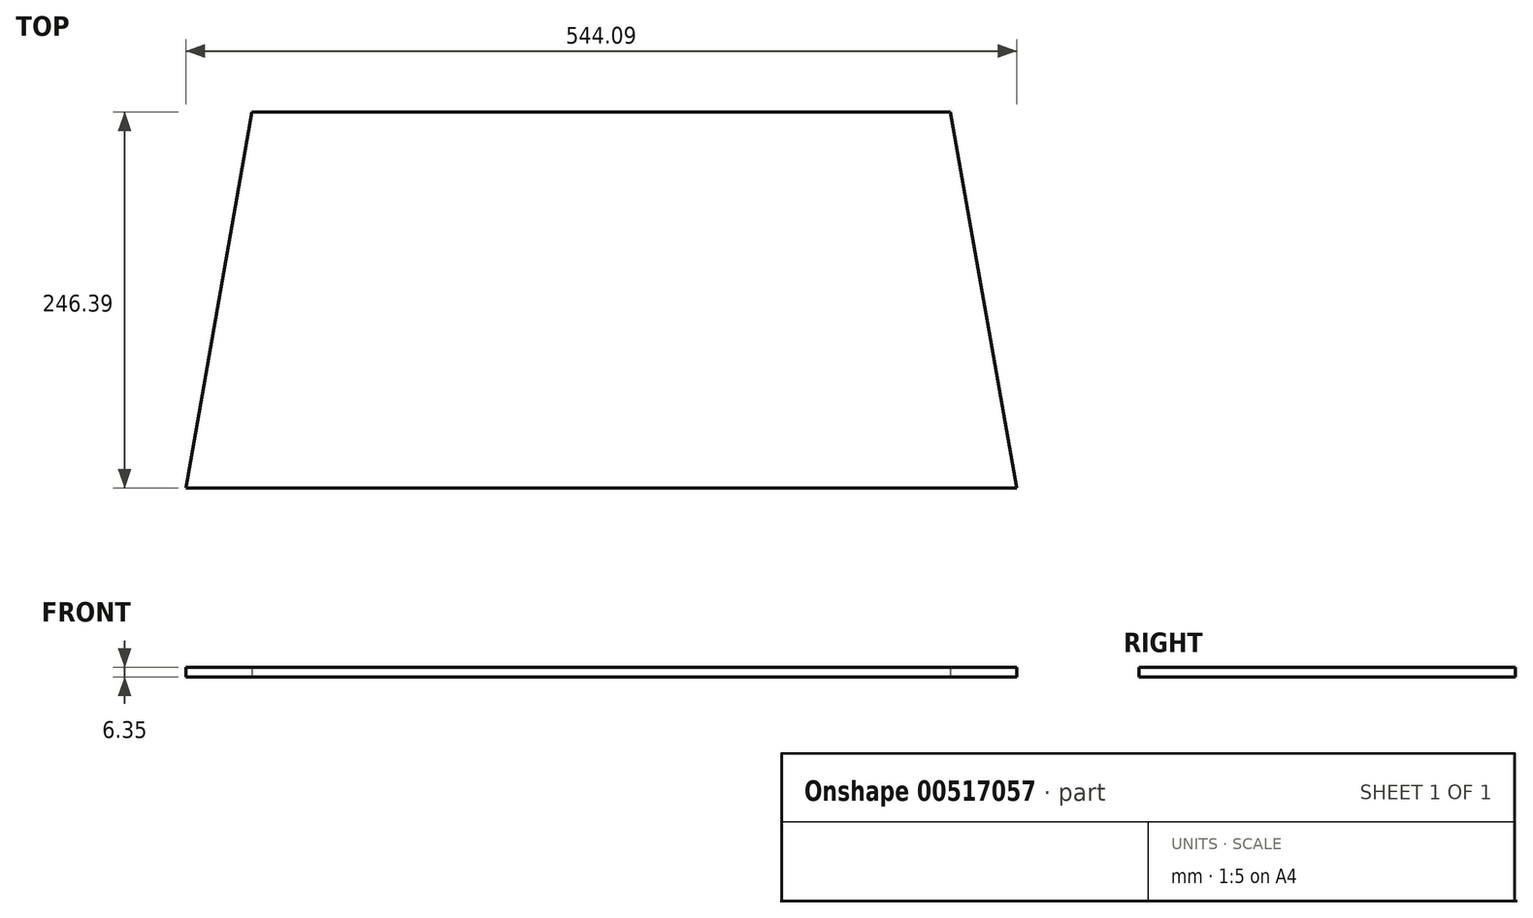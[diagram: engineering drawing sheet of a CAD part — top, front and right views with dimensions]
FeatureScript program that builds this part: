
annotation { "Feature Type Name" : "Feature", "Feature Type Description" : "" }
export const myFeature = defineFeature(function(context is Context, id is Id, definition is map)
    precondition{}
    {
        {
            var Q0;
            Q0=qCreatedBy(makeId("Top.planeOp"),FACE);
            var sketch = newSketch(context, id + "F0", { "sketchPlane" : qUnion([Q0])});
            skLineSegment(sketch, "E0.bottom", {"start": v(-256.12, 169.6) * mm, "end": v(201.08, 169.6) * mm});
            skLineSegment(sketch, "E0.right", {"start": v(201.08, 169.6) * mm, "end": v(244.53, -76.8) * mm});
            skLineSegment(sketch, "E1", {"start": v(-256.12, 169.6) * mm, "end": v(-299.56, -76.8) * mm});
            skLineSegment(sketch, "E2", {"start": v(-299.56, -76.8) * mm, "end": v(244.53, -76.8) * mm});
            skSolve(sketch);
        }
        {
            var Q0;
            Q0=makeQuery(id+"F0.imprint","IMPRINT",FACE,{"disambiguationData":[TD([[makeQuery(id+"F0.imprint","IMPRINT",EDGE,{"derivedFrom":sQuery(id+"F0.wireOp",EDGE,"E0.bottom")}),-1.0]])]});
            extrude(context, id + "F1", {"entities" : qUnion([Q0]), "depth" : 12.7 * mm, "offsetDistance" : 25.4 * mm});
        }
        {
            var Q0;
            Q0=makeQuery(id+"F1.opExtrude","CAP_FACE",FACE,{"disambiguationData":[OSD([sQuery(id+"F0.wireOp",EDGE,"E0.bottom"),sQuery(id+"F0.wireOp",EDGE,"E0.right"),sQuery(id+"F0.wireOp",EDGE,"E1"),sQuery(id+"F0.wireOp",EDGE,"E2")])],"isStart":false});
            extrude(context, id + "F2", {"entities" : qUnion([Q0]), "operationType" : NewBodyOperationType.ADD, "depth" : -6.35 * mm, "offsetDistance" : 25.4 * mm});
        }
        {
            var Q0;
            Q0=makeQuery(id+"F1.opExtrude","CAP_FACE",FACE,{"disambiguationData":[OSD([sQuery(id+"F0.wireOp",EDGE,"E0.bottom"),sQuery(id+"F0.wireOp",EDGE,"E0.right"),sQuery(id+"F0.wireOp",EDGE,"E1"),sQuery(id+"F0.wireOp",EDGE,"E2")])],"isStart":false});
            extrude(context, id + "F3", {"entities" : qUnion([Q0]), "operationType" : NewBodyOperationType.ADD, "depth" : -6.35 * mm, "offsetDistance" : 25.4 * mm});
        }
        {
            var Q0;
            Q0=makeQuery(id+"F1.opExtrude","CAP_FACE",FACE,{"disambiguationData":[OSD([sQuery(id+"F0.wireOp",EDGE,"E0.bottom"),sQuery(id+"F0.wireOp",EDGE,"E0.right"),sQuery(id+"F0.wireOp",EDGE,"E1"),sQuery(id+"F0.wireOp",EDGE,"E2")])],"isStart":false});
            extrude(context, id + "F4", {"entities" : qUnion([Q0]), "operationType" : NewBodyOperationType.REMOVE, "depth" : -6.35 * mm, "offsetDistance" : 25.4 * mm});
        }
    });
